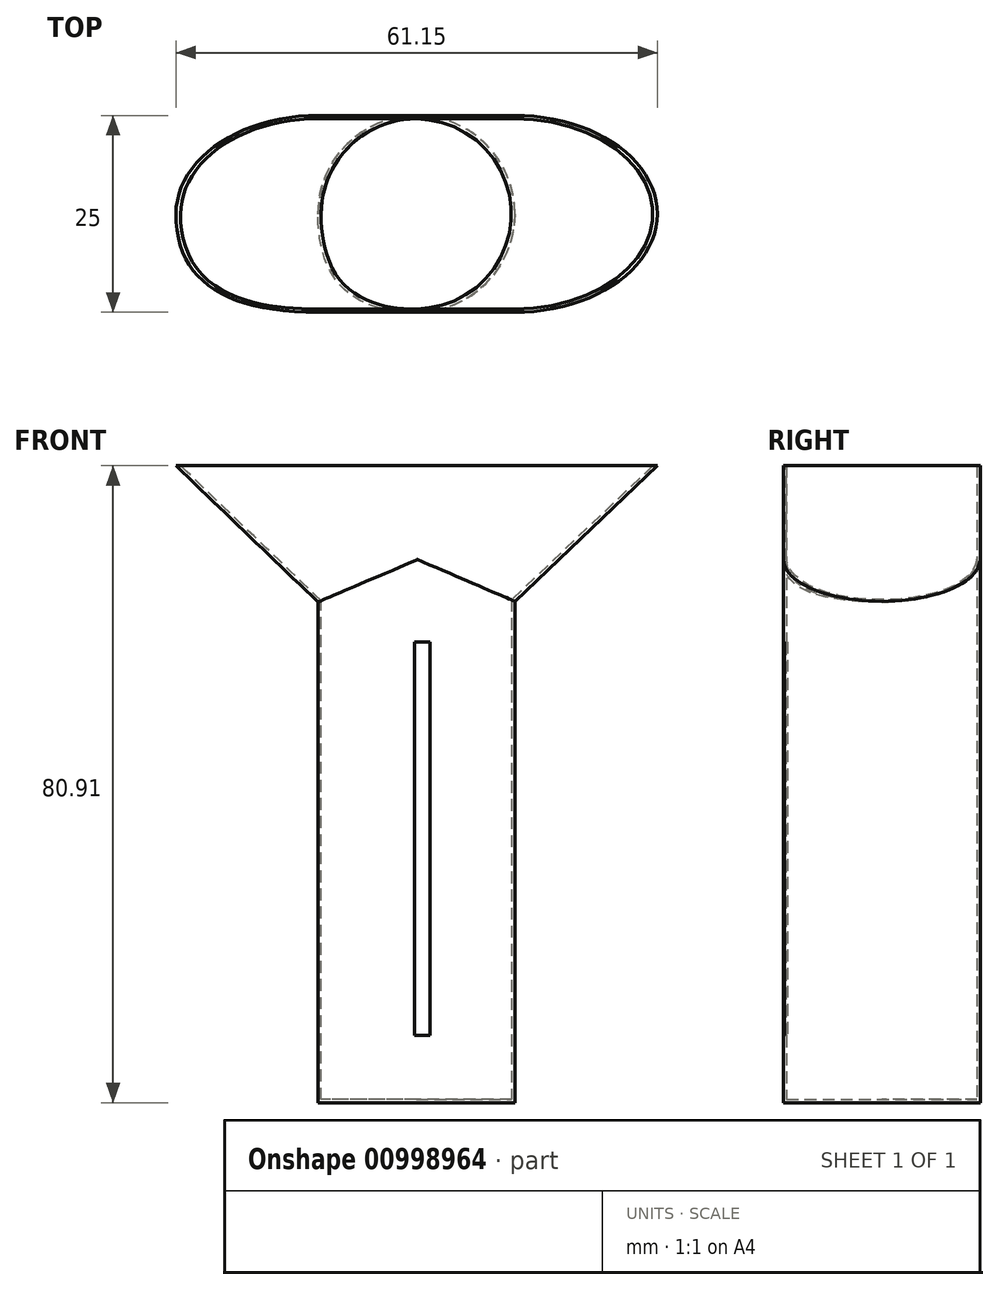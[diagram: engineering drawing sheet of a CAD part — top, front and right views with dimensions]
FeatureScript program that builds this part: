
annotation { "Feature Type Name" : "Feature", "Feature Type Description" : "" }
export const myFeature = defineFeature(function(context is Context, id is Id, definition is map)
    precondition{}
    {
        {
            var Q0;
            Q0=qCreatedBy(makeId("Front.planeOp"),FACE);
            var sketch = newSketch(context, id + "F0", { "sketchPlane" : qUnion([Q0])});
            skLineSegment(sketch, "E0", {"start": v(-13.26, 4.82) * mm, "end": v(-13.26, -58.78) * mm});
            skLineSegment(sketch, "E1", {"start": v(-13.26, -58.78) * mm, "end": v(11.74, -58.78) * mm});
            skLineSegment(sketch, "E2", {"start": v(11.74, -58.78) * mm, "end": v(11.74, 4.91) * mm});
            skLineSegment(sketch, "E3", {"start": v(11.74, 4.91) * mm, "end": v(29.86, 22.13) * mm});
            skLineSegment(sketch, "E4", {"start": v(29.86, 22.13) * mm, "end": v(-31.3, 22.13) * mm});
            skLineSegment(sketch, "E5", {"start": v(-31.3, 22.13) * mm, "end": v(-13.26, 4.82) * mm});
            skSolve(sketch);
        }
        {
            var Q0;
            Q0=makeQuery(id+"F0.imprint","IMPRINT",FACE,{"disambiguationData":[TD([[makeQuery(id+"F0.imprint","IMPRINT",EDGE,{"derivedFrom":sQuery(id+"F0.wireOp",EDGE,"E0")}),1.0]])]});
            extrude(context, id + "F1", {"entities" : qUnion([Q0]), "endBound" : BoundingType.SYMMETRIC, "depth" : 25 * mm, "offsetDistance" : 25 * mm});
        }
        {
            var Q0;
            Q0=makeQuery(id+"F1.opExtrude","CAP_EDGE",EDGE,{"disambiguationData":[OSD([sQuery(id+"F0.wireOp",EDGE,"E0")])],"isStart":false});
            var Q1;
            Q1=makeQuery(id+"F1.opExtrude","CAP_EDGE",EDGE,{"disambiguationData":[OSD([sQuery(id+"F0.wireOp",EDGE,"E5")])],"isStart":false});
            fillet(context, id + "F2", {"entities" : qUnion([Q0, Q1]), "radius" : 12.5 * mm, "rho" : 0.5, "crossSection" : FilletCrossSection.CONIC, "allowEdgeOverflow" : false});
        }
        {
            var Q0;
            Q0=makeQuery(id+"F1.opExtrude","CAP_EDGE",EDGE,{"disambiguationData":[OSD([sQuery(id+"F0.wireOp",EDGE,"E5")])],"isStart":true});
            var Q1;
            Q1=makeQuery(id+"F1.opExtrude","CAP_EDGE",EDGE,{"disambiguationData":[OSD([sQuery(id+"F0.wireOp",EDGE,"E0")])],"isStart":true});
            fillet(context, id + "F3", {"entities" : qUnion([Q0, Q1]), "radius" : 12.5 * mm, "tangentPropagation" : true, "allowEdgeOverflow" : false});
        }
        {
            var Q0;
            Q0=makeQuery(id+"F1.opExtrude","CAP_EDGE",EDGE,{"disambiguationData":[OSD([sQuery(id+"F0.wireOp",EDGE,"E3")])],"isStart":false});
            var Q1;
            Q1=makeQuery(id+"F1.opExtrude","CAP_EDGE",EDGE,{"disambiguationData":[OSD([sQuery(id+"F0.wireOp",EDGE,"E2")])],"isStart":false});
            fillet(context, id + "F4", {"entities" : qUnion([Q0, Q1]), "radius" : 12.5 * mm, "tangentPropagation" : true, "allowEdgeOverflow" : false});
        }
        {
            var Q0;
            Q0=makeQuery(id+"F1.opExtrude","CAP_EDGE",EDGE,{"disambiguationData":[OSD([sQuery(id+"F0.wireOp",EDGE,"E3")])],"isStart":true});
            var Q1;
            Q1=makeQuery(id+"F1.opExtrude","CAP_EDGE",EDGE,{"disambiguationData":[OSD([sQuery(id+"F0.wireOp",EDGE,"E2")])],"isStart":true});
            fillet(context, id + "F5", {"entities" : qUnion([Q0, Q1]), "radius" : 12.5 * mm, "tangentPropagation" : true, "allowEdgeOverflow" : false});
        }
        {
            var Q0;
            Q0=makeQuery(id+"F1.opExtrude","SWEPT_FACE",FACE,{"disambiguationData":[OSD([sQuery(id+"F0.wireOp",EDGE,"E4")])]});
            shell(context, id + "F6", {"entities" : qUnion([Q0]), "thickness" : .4 * mm});
        }
        {
            var Q0;
            Q0=qCreatedBy(makeId("Front.planeOp"),FACE);
            var sketch = newSketch(context, id + "F7", { "sketchPlane" : qUnion([Q0])});
            skLineSegment(sketch, "E6.bottom", {"start": v(-1, -0.23) * mm, "end": v(1, -0.23) * mm});
            skLineSegment(sketch, "E6.top", {"start": v(-1, -50.23) * mm, "end": v(1, -50.23) * mm});
            skLineSegment(sketch, "E6.left", {"start": v(-1, -0.23) * mm, "end": v(-1, -50.23) * mm});
            skLineSegment(sketch, "E6.right", {"start": v(1, -0.23) * mm, "end": v(1, -50.23) * mm});
            skPoint(sketch, "E6.middle", {"position": v(0, -25.23) * mm});
            skSolve(sketch);
        }
        {
            var Q0;
            Q0=makeQuery(id+"F7.imprint","IMPRINT",FACE,{"disambiguationData":[TD([[makeQuery(id+"F7.imprint","IMPRINT",EDGE,{"derivedFrom":sQuery(id+"F7.wireOp",EDGE,"E6.bottom")}),-1.0]])]});
            extrude(context, id + "F8", {"entities" : qUnion([Q0]), "operationType" : NewBodyOperationType.REMOVE, "endBound" : BoundingType.THROUGH_ALL, "depth" : 25 * mm, "offsetDistance" : 25 * mm});
        }
    });
